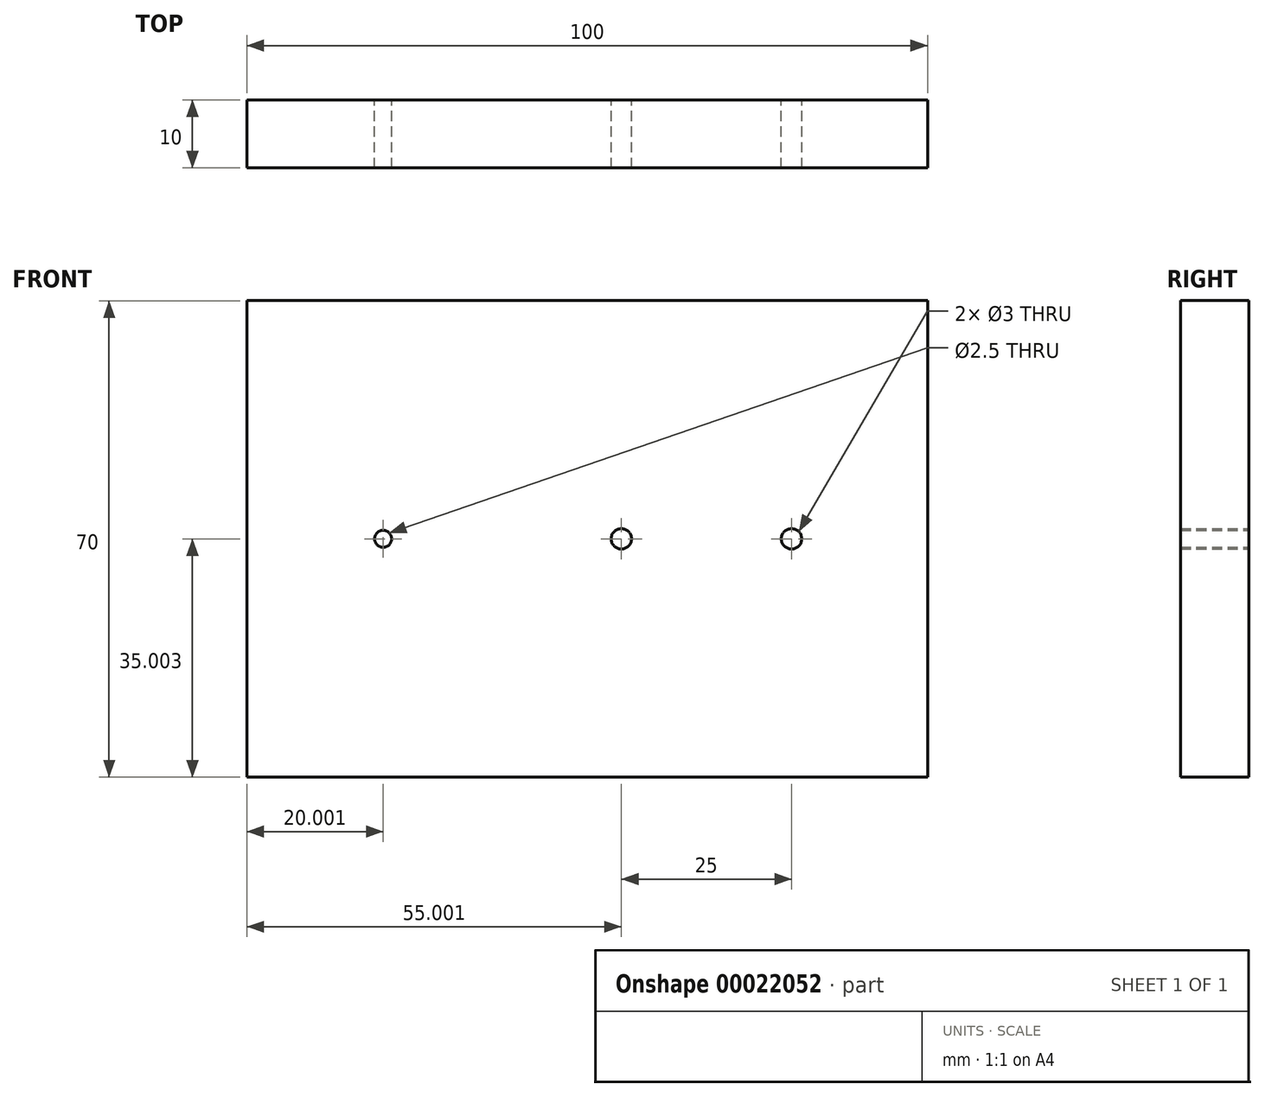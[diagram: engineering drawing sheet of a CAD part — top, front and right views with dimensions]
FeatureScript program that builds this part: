
annotation { "Feature Type Name" : "Feature", "Feature Type Description" : "" }
export const myFeature = defineFeature(function(context is Context, id is Id, definition is map)
    precondition{}
    {
        {
            var Q0;
            Q0=qCreatedBy(makeId("Front.planeOp"),FACE);
            var sketch = newSketch(context, id + "F0", { "sketchPlane" : qUnion([Q0])});
            skLineSegment(sketch, "E0.bottom", {"start": v(-25.15, 26.18) * mm, "end": v(74.85, 26.18) * mm});
            skLineSegment(sketch, "E0.top", {"start": v(-25.15, -43.82) * mm, "end": v(74.85, -43.82) * mm});
            skLineSegment(sketch, "E0.left", {"start": v(-25.15, 26.18) * mm, "end": v(-25.15, -43.82) * mm});
            skLineSegment(sketch, "E0.right", {"start": v(74.85, 26.18) * mm, "end": v(74.85, -43.82) * mm});
            skLineSegment(sketch, "E1.bottom", {"start": v(1.8, -43.82) * mm, "end": v(1.8, -43.82) * mm});
            skLineSegment(sketch, "E1.top", {"start": v(1.8, -48.24) * mm, "end": v(1.8, -48.24) * mm});
            skLineSegment(sketch, "E2", {"start": v(-25.15, -8.82) * mm, "end": v(-5.15, -8.82) * mm});
            skLineSegment(sketch, "E3", {"start": v(-5.15, -8.82) * mm, "end": v(14.85, -8.82) * mm});
            skCircle(sketch, "E4", {"center": v(-5.15, -8.82) * mm, "radius": 1.25 * mm});
            skLineSegment(sketch, "E5", {"start": v(14.85, -8.82) * mm, "end": v(29.85, -8.82) * mm});
            skCircle(sketch, "E6", {"center": v(29.85, -8.82) * mm, "radius": 1.5 * mm});
            skLineSegment(sketch, "E7", {"start": v(29.85, -8.82) * mm, "end": v(44.85, -8.82) * mm});
            skLineSegment(sketch, "E8", {"start": v(44.85, -8.82) * mm, "end": v(54.85, -8.82) * mm});
            skCircle(sketch, "E9", {"center": v(54.85, -8.82) * mm, "radius": 1.5 * mm});
            skLineSegment(sketch, "E10", {"start": v(20.18, -8.82) * mm, "end": v(54.85, -8.82) * mm});
            skSolve(sketch);
        }
        {
            var Q0;
            Q0=makeQuery(id+"F0.imprint","IMPRINT",FACE,{"disambiguationData":[TD([[makeQuery(id+"F0.imprint","IMPRINT",EDGE,{"derivedFrom":sQuery(id+"F0.wireOp",EDGE,"E0.bottom")}),-1.0]])]});
            extrude(context, id + "F1", {"entities" : qUnion([Q0]), "depth" : 10 * mm});
        }
    });
